# Revit family: RONDO-FLAP-R95
name_source: partatom
category: Осветительные приборы
revit_build: Autodesk Revit 2017 (Build: 20160225_1515(x64)
units: mm (PartAtom-declared; Revit-internal decimal feet)

## family parameters
Всегда вертикально = Да
Источник света = Нет
На основе рабочей плоскости = Нет
Общий = Нет
При загрузке вырезать с полостями = Нет
Размер круглого соединителя = Использовать диаметр
Тип детали = Нормальный
Точка расчета площади = Нет

## types (4) — shared parameters
ADSK_Единица измерения = шт.
ADSK_Завод-изготовитель = ARLIGHT
ADSK_Классификация нагрузок = Освещение
ADSK_Количество фаз = 1
ADSK_Количество фаз числовое = 1
ADSK_Коэффициент мощности = 0.94
ADSK_Масса_Текст = 0.793
ADSK_Наименование = Светильник
ADSK_Напряжение = 230 В
ADSK_Номинальная мощность = 16 Вт
ADSK_Полная мощность = 17 В·А
ADSK_Размер_Высота = 105 мм
ADSK_Размер_Диаметр = 95 мм
ADSK_Ток = 0 А
ARL_Драйвер = Встроенный (400mA, 30-42V)
ARL_Индекс цветопередачи = >90
ARL_Класс защиты от поражения электрическим током = I
ARL_Класс пылевлагозащиты = IP40
ARL_Область использования = Для основного освещения и декоративного светового оформления в жилых, офисных, торговых помещениях
ARL_Рабочая температура окружающей среды = -10...+50 °C
ARL_Серия = RONDO FLAP
ARL_Способ монтажа = Накладной
ARL_Тип товара = Светильник
ARL_Угол обзора = 110°
URL = https://arlight.ru
Группа модели = Светильники
Изготовитель = ARLIGHT
Изготовитель (сайт) = www.arlight.ru
Изготовитель (телефон) = 8 800 505 26 29
Полная установленная мощность = 17 В·А
Разработчик = НТЦ Конструктор
Разработчик (URL) = https://constructor.ru
Разработчик (телефон) = +7 (495) 781-05-35

## per-type parameters (varying)
| type | ADSK_Код изделия | ADSK_Марка | ARL_Материал корпуса | ARL_Обозначение корпуса | ARL_Цвет покрытия | ARL_Цвет свечения | Исходная интенсивность (лм) | Комментарии к типоразмеру | Описание | Фотометрия | Цветовая температура (К) |
| 026481 Светильник SP-RONDO-FLAP-R95-16W Day4000 (WH, 110 deg) | Арт. 026481 | SP-RONDO-FLAP-R95-16W Day4000 | Металл, белый | Корпус круглый, металл, цвет белый | Белый | Дневной 4000K | 1120 | Арт. 026481 | Накладной откидной светильник 16 Вт, белый круглый корпус. Цвет ДНЕВНОЙ 4000K, св.поток 1120лм, CRI(Ra)>90, угол 110°. Размер светильника Ф95x55 мм, размер чаши Ф95x45 мм. Питание AC220-240V, 16 Вт, драйвер встроенный (400mA, 30-42V). Поворачивается вокруг своей оси на 350° и отклоняется на 90° | RONDO-FLAP-R95 IES Data : 026481_SP-RONDO-FLAP-R95-16W Day4000 (WH, 110 deg) | 4000 |
| 028156 Светильник SP-RONDO-FLAP-R95-16W Warm3000 (WH, 110 deg) | Арт. 028156 | SP-RONDO-FLAP-R95-16W Warm3000 | Металл, белый | Корпус круглый, металл, цвет белый | Белый | Теплый 3000K | 1080 | Арт. 028156 | Накладной откидной светильник 16 Вт, белый круглый корпус. Цвет ТЕПЛЫЙ 3000K, св.поток 1080лм, CRI(Ra)>90, угол 110°. Размер светильника Ф95x55 мм, размер чаши Ф95x45 мм. Питание AC220-240V, 16 Вт, драйвер встроенный (400mA, 30-42V). Поворачивается вокруг своей оси на 350° и отклоняется на 90° | RONDO-FLAP-R95 IES Data : 028156_SP-RONDO-FLAP-R95-16W Warm3000 (WH, 110 deg) | 3000 |
| 028157 Светильник SP-RONDO-FLAP-R95-16W Day4000 (BK, 110 deg) | Арт. 028157 | SP-RONDO-FLAP-R95-16W Day4000 | Металл, чёрный | Корпус круглый, металл, цвет черный | Черный | Дневной 4000K | 1120 | Арт. 028157 | Накладной откидной светильник 16 Вт, черный круглый корпус. Цвет ДНЕВНОЙ 4000K, св.поток 1120лм, CRI(Ra)>90, угол 110°. Размер светильника Ф95x55 мм, размер чаши Ф95x45 мм. Питание AC220-240V, 16 Вт, драйвер встроенный (400mA, 30-42V). Поворачивается вокруг своей оси на 350° и отклоняется на 90° | RONDO-FLAP-R95 IES Data : 028157_SP-RONDO-FLAP-R95-16W Day4000 (BK, 110 deg) | 4000 |
| 028158 Светильник SP-RONDO-FLAP-R95-16W Warm3000 (BK, 110 deg) | Арт. 028158 | SP-RONDO-FLAP-R95-16W Warm3000 | Металл, чёрный | Корпус круглый, металл, цвет черный | Черный | Теплый 3000K | 1080 | Арт. 028158 | Накладной откидной светильник 16 Вт, черный круглый корпус. Цвет ТЕПЛЫЙ 3000K, св.поток 1080лм, CRI(Ra)>90, угол 110°. Размер светильника Ф95x55 мм, размер чаши Ф95x45 мм. Питание AC220-240V, 16 Вт, драйвер встроенный (400mA, 30-42V). Поворачивается вокруг своей оси на 350° и отклоняется на 90° | RONDO-FLAP-R95 IES Data : 028158_SP-RONDO-FLAP-R95-16W Warm3000 (BK, 110 deg) | 3000 |

## geometry (parser evidence)
native form markers: Sweep x3
no freeform markers — native parametric forms only
